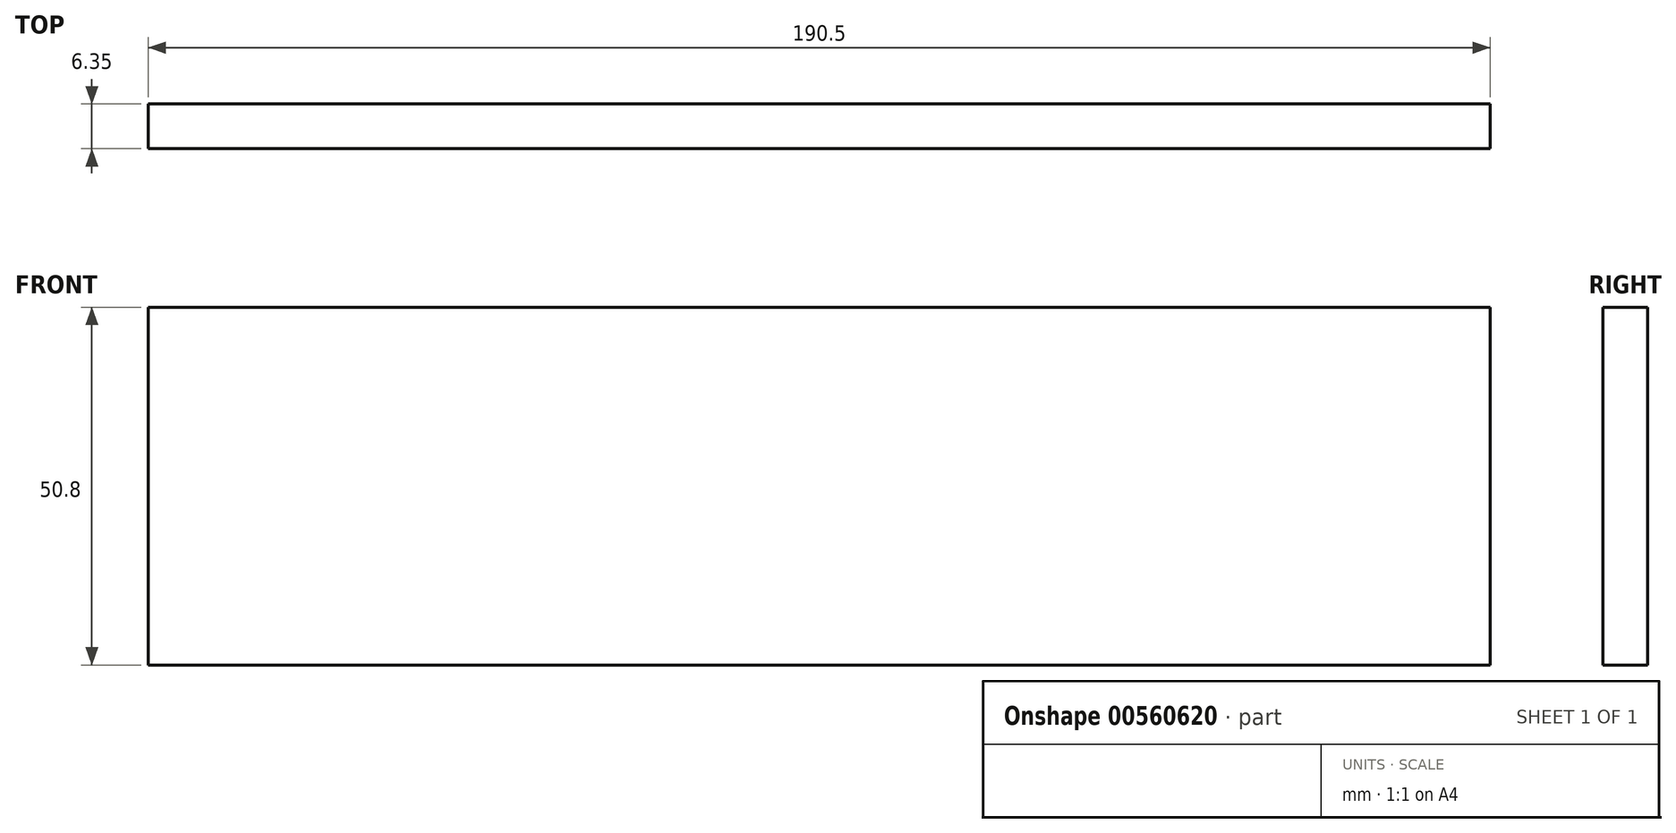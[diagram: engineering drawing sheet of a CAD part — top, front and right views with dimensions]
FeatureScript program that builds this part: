
annotation { "Feature Type Name" : "Feature", "Feature Type Description" : "" }
export const myFeature = defineFeature(function(context is Context, id is Id, definition is map)
    precondition{}
    {
        {
            var Q0;
            Q0=qCreatedBy(makeId("Front.planeOp"),FACE);
            var sketch = newSketch(context, id + "F0", { "sketchPlane" : qUnion([Q0])});
            skLineSegment(sketch, "E0.bottom", {"start": v(-95.25, 25.4) * mm, "end": v(95.25, 25.4) * mm});
            skLineSegment(sketch, "E0.top", {"start": v(-95.25, -25.4) * mm, "end": v(95.25, -25.4) * mm});
            skLineSegment(sketch, "E0.left", {"start": v(-95.25, 25.4) * mm, "end": v(-95.25, -25.4) * mm});
            skLineSegment(sketch, "E0.right", {"start": v(95.25, 25.4) * mm, "end": v(95.25, -25.4) * mm});
            skSolve(sketch);
        }
        {
            var Q0;
            Q0=makeQuery(id+"F0.imprint","IMPRINT",FACE,{"disambiguationData":[TD([[makeQuery(id+"F0.imprint","IMPRINT",EDGE,{"derivedFrom":sQuery(id+"F0.wireOp",EDGE,"E0.bottom")}),-1.0]])]});
            extrude(context, id + "F1", {"entities" : qUnion([Q0]), "depth" : 6.35 * mm, "offsetDistance" : 25.4 * mm});
        }
    });
